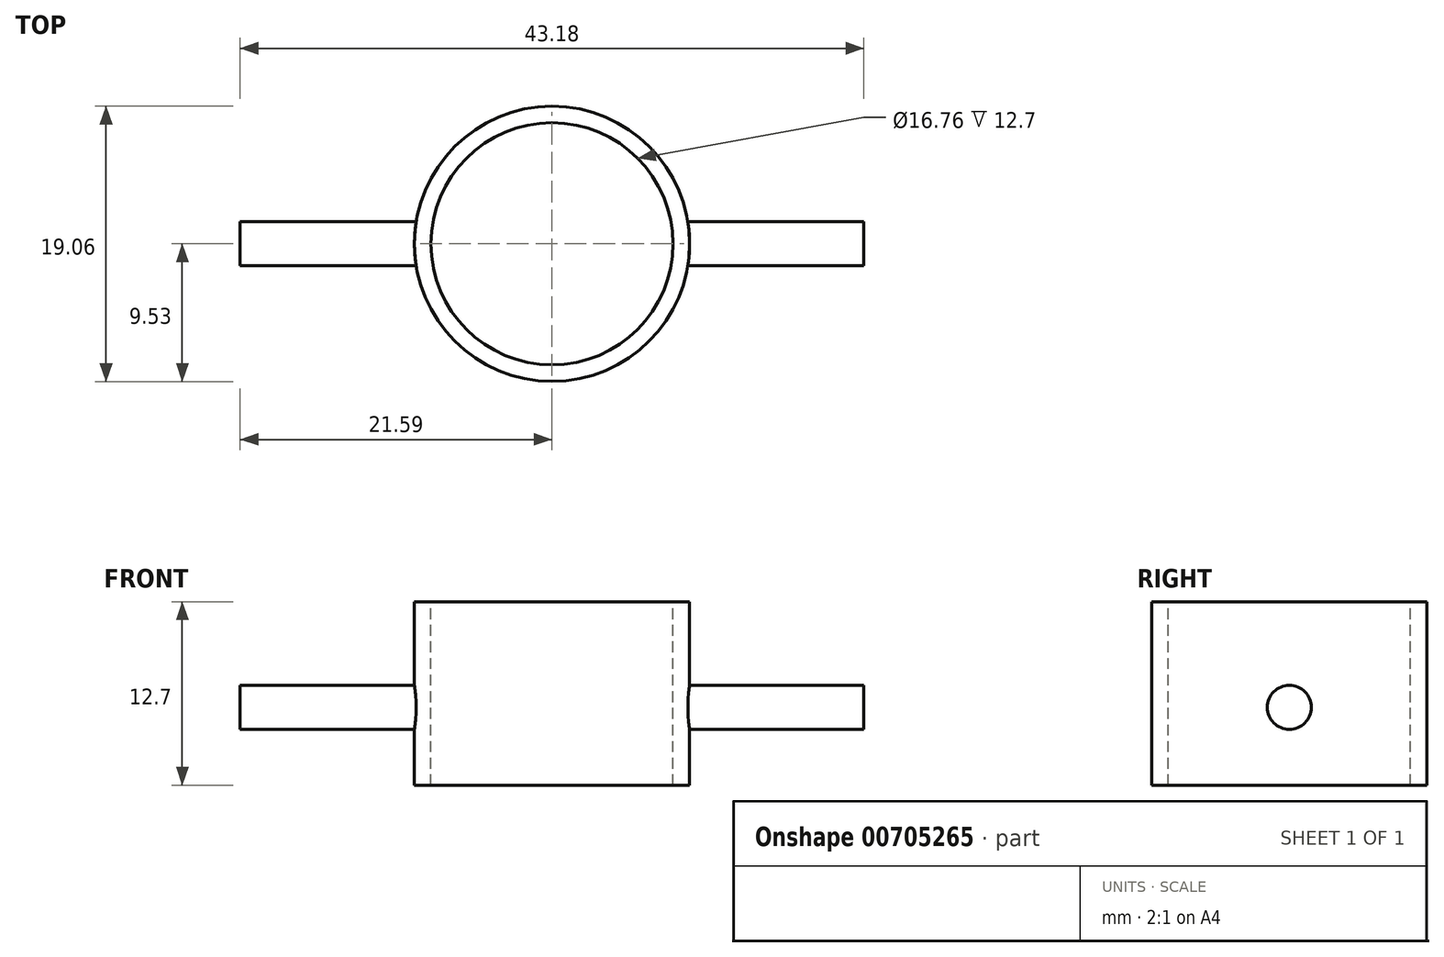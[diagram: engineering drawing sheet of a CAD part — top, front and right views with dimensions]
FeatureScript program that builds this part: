
annotation { "Feature Type Name" : "Feature", "Feature Type Description" : "" }
export const myFeature = defineFeature(function(context is Context, id is Id, definition is map)
    precondition{}
    {
        {
            var Q0;
            Q0=qCreatedBy(makeId("Top.planeOp"),FACE);
            var sketch = newSketch(context, id + "F0", { "sketchPlane" : qUnion([Q0])});
            skCircle(sketch, "E0", {"center": v(0, 0) * mm, "radius": 9.53 * mm});
            skSolve(sketch);
        }
        {
            var Q0;
            Q0 = qSketchRegion(id + "F0", true);
            extrude(context, id + "F1", {"entities" : qUnion([Q0]), "depth" : 12.7 * mm, "offsetDistance" : 25.4 * mm});
        }
        {
            var Q0;
            Q0=makeQuery(id+"F1.opExtrude","CAP_FACE",FACE,{"disambiguationData":[OSD([sQuery(id+"F0.wireOp",EDGE,"E0")])],"isStart":false});
            var sketch = newSketch(context, id + "F2", { "sketchPlane" : qUnion([Q0])});
            skCircle(sketch, "E1", {"center": v(0, 0) * mm, "radius": 8.38 * mm});
            skSolve(sketch);
        }
        {
            var Q0;
            Q0 = qSketchRegion(id + "F2", true);
            extrude(context, id + "F3", {"entities" : qUnion([Q0]), "operationType" : NewBodyOperationType.REMOVE, "oppositeDirection" : true, "depth" : 25.4 * mm, "offsetDistance" : 25.4 * mm});
        }
        {
            var Q0;
            Q0=qCreatedBy(makeId("Right.planeOp"),FACE);
            cPlane(context, id + "F4", {"entities" : qUnion([Q0]), "cplaneType" : CPlaneType.OFFSET, "offset" : 8.9 * mm, "width" : 152.4 * mm, "height" : 152.4 * mm});
        }
        {
            var Q0;
            Q0=qCreatedBy(id+"F4.planeOp",FACE);
            var sketch = newSketch(context, id + "F5", { "sketchPlane" : qUnion([Q0])});
            skCircle(sketch, "E2", {"center": v(0, 5.4) * mm, "radius": 1.52 * mm});
            skSolve(sketch);
        }
        {
            var Q0;
            Q0 = qSketchRegion(id + "F5", true);
            extrude(context, id + "F6", {"entities" : qUnion([Q0]), "operationType" : NewBodyOperationType.ADD, "depth" : 12.7 * mm, "offsetDistance" : 25.4 * mm});
        }
        {
            var Q0;
            Q0=makeQuery(id+"F1.opExtrude","SWEPT_BODY",BODY,{"disambiguationData":[OSD([sQuery(id+"F0.wireOp",EDGE,"E0")])]});
            var Q1;
            Q1=qCreatedBy(makeId("Right.planeOp"),FACE);
            mirror(context, id + "F7", {"operationType" : NewBodyOperationType.ADD, "entities" : qUnion([Q0]), "mirrorPlane" : qUnion([Q1])});
        }
    });
